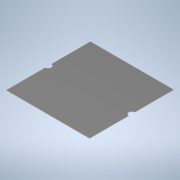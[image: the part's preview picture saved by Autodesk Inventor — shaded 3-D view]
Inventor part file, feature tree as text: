
AUTODESK INVENTOR PART (.ipt)
format: ipt  version: 2022 (Build 260153000, 153)  size: 110,080 bytes
history: native  units: in
note: dims shown in document units (in); Inventor stores cm internally (conversion verified against a paired STEP export)
features: extrude x2, sketch x2
ambient origin geometry x8: Origin, YZ Plane, XZ Plane, XY Plane, X Axis, Y Axis, Z Axis, Center Point
bodies: Solid1 (feature_tree)
feature tree (4):
  extrude  "Extrusion1"  Depth=1.6378in
  extrude  "Extrusion2"  Depth=0.0591in
  sketch  "Sketch1"  dims[d0=1.6535in d1=1.6378in]
  sketch  "Sketch2"  dims[d2=0.0031in d3=0.0in d5=0.0591in d6=0.0in d7=0.0in]
